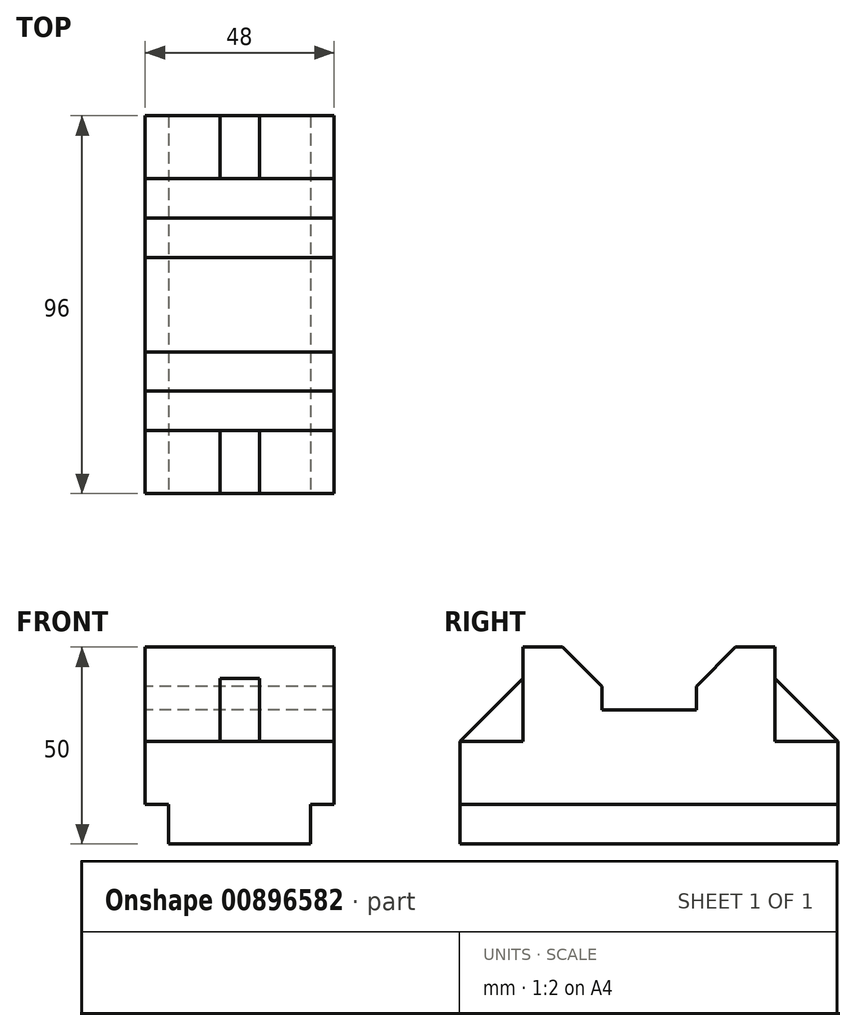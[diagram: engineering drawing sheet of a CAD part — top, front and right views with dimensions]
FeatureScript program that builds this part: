
annotation { "Feature Type Name" : "Feature", "Feature Type Description" : "" }
export const myFeature = defineFeature(function(context is Context, id is Id, definition is map)
    precondition{}
    {
        {
            var Q0;
            Q0=qCreatedBy(makeId("Front.planeOp"),FACE);
            var sketch = newSketch(context, id + "F0", { "sketchPlane" : qUnion([Q0])});
            skLineSegment(sketch, "E0.bottom", {"start": v(-24, 25) * mm, "end": v(24, 25) * mm});
            skLineSegment(sketch, "E0.top", {"start": v(-24, -25) * mm, "end": v(24, -25) * mm});
            skLineSegment(sketch, "E0.left", {"start": v(-24, 25) * mm, "end": v(-24, -25) * mm});
            skLineSegment(sketch, "E0.right", {"start": v(24, 25) * mm, "end": v(24, -25) * mm});
            skSolve(sketch);
        }
        {
            var Q0;
            Q0 = qSketchRegion(id + "F0", true);
            extrude(context, id + "F1", {"entities" : qUnion([Q0]), "endBound" : BoundingType.SYMMETRIC, "depth" : 96 * mm, "offsetDistance" : 25 * mm});
        }
        {
            var Q0;
            Q0=makeQuery(id+"F1.opExtrude","CAP_FACE",FACE,{"disambiguationData":[OSD([sQuery(id+"F0.wireOp",EDGE,"E0.bottom"),sQuery(id+"F0.wireOp",EDGE,"E0.top"),sQuery(id+"F0.wireOp",EDGE,"E0.left"),sQuery(id+"F0.wireOp",EDGE,"E0.right")])],"isStart":false});
            var sketch = newSketch(context, id + "F2", { "sketchPlane" : qUnion([Q0])});
            skLineSegment(sketch, "E1.bottom", {"start": v(-24, -25) * mm, "end": v(-18, -25) * mm});
            skLineSegment(sketch, "E1.top", {"start": v(-24, -15) * mm, "end": v(-18, -15) * mm});
            skLineSegment(sketch, "E1.left", {"start": v(-24, -25) * mm, "end": v(-24, -15) * mm});
            skLineSegment(sketch, "E1.right", {"start": v(-18, -25) * mm, "end": v(-18, -15) * mm});
            skLineSegment(sketch, "E2.bottom", {"start": v(24, -25) * mm, "end": v(18, -25) * mm});
            skLineSegment(sketch, "E2.top", {"start": v(24, -15) * mm, "end": v(18, -15) * mm});
            skLineSegment(sketch, "E2.left", {"start": v(24, -25) * mm, "end": v(24, -15) * mm});
            skLineSegment(sketch, "E2.right", {"start": v(18, -25) * mm, "end": v(18, -15) * mm});
            skSolve(sketch);
        }
        {
            var Q0;
            Q0 = qSketchRegion(id + "F2", true);
            extrude(context, id + "F3", {"entities" : qUnion([Q0]), "operationType" : NewBodyOperationType.REMOVE, "endBound" : BoundingType.THROUGH_ALL, "oppositeDirection" : true, "depth" : 25 * mm, "offsetDistance" : 25 * mm});
        }
        {
            var Q0;
            Q0=makeQuery(id+"F1.opExtrude","CAP_FACE",FACE,{"disambiguationData":[OSD([sQuery(id+"F0.wireOp",EDGE,"E0.bottom"),sQuery(id+"F0.wireOp",EDGE,"E0.top"),sQuery(id+"F0.wireOp",EDGE,"E0.left"),sQuery(id+"F0.wireOp",EDGE,"E0.right")])],"isStart":false});
            var sketch = newSketch(context, id + "F4", { "sketchPlane" : qUnion([Q0])});
            skLineSegment(sketch, "E3", {"start": v(-24, 1) * mm, "end": v(-5, 1) * mm});
            skLineSegment(sketch, "E4", {"start": v(-5, 1) * mm, "end": v(-5, 25) * mm});
            skLineSegment(sketch, "E5", {"start": v(-5, 25) * mm, "end": v(-24, 25) * mm});
            skLineSegment(sketch, "E6", {"start": v(-24, 25) * mm, "end": v(-24, 1) * mm});
            skLineSegment(sketch, "E7", {"start": v(-5, 1) * mm, "end": v(5, 1) * mm, "construction": true});
            skLineSegment(sketch, "E8", {"start": v(5, 1) * mm, "end": v(24, 1) * mm});
            skLineSegment(sketch, "E9", {"start": v(24, 1) * mm, "end": v(24, 25) * mm});
            skLineSegment(sketch, "E10", {"start": v(24, 25) * mm, "end": v(5, 25) * mm});
            skLineSegment(sketch, "E11", {"start": v(5, 25) * mm, "end": v(5, 1) * mm});
            skSolve(sketch);
        }
        {
            var Q0;
            Q0 = qSketchRegion(id + "F4", true);
            extrude(context, id + "F5", {"entities" : qUnion([Q0]), "operationType" : NewBodyOperationType.REMOVE, "oppositeDirection" : true, "depth" : 16 * mm, "offsetDistance" : 25 * mm});
        }
        {
            var Q0;
            Q0=makeQuery(id+"F5.boolean.opBoolean","COPY",FACE,{"derivedFrom":makeQuery(id+"F5.opExtrude","SWEPT_FACE",FACE,{"disambiguationData":[OSD([sQuery(id+"F4.wireOp",EDGE,"E4")])]})});
            var sketch = newSketch(context, id + "F6", { "sketchPlane" : qUnion([Q0])});
            skLineSegment(sketch, "E12", {"start": v(32, 1) * mm, "end": v(48, 1) * mm, "construction": true});
            skLineSegment(sketch, "E13", {"start": v(48, 1) * mm, "end": v(32, 17) * mm});
            skLineSegment(sketch, "E14", {"start": v(32, 17) * mm, "end": v(32, 1) * mm, "construction": true});
            skLineSegment(sketch, "E15", {"start": v(48, 1) * mm, "end": v(48, 25) * mm});
            skLineSegment(sketch, "E16", {"start": v(48, 25) * mm, "end": v(32, 25) * mm});
            skLineSegment(sketch, "E17", {"start": v(32, 25) * mm, "end": v(32, 17) * mm});
            skSolve(sketch);
        }
        {
            var Q0;
            Q0 = qSketchRegion(id + "F6", true);
            extrude(context, id + "F7", {"entities" : qUnion([Q0]), "operationType" : NewBodyOperationType.REMOVE, "endBound" : BoundingType.THROUGH_ALL, "oppositeDirection" : true, "depth" : 25 * mm, "offsetDistance" : 25 * mm});
        }
        {
            var Q0;
            Q0=makeQuery(id+"F1.opExtrude","SWEPT_FACE",FACE,{"disambiguationData":[OSD([sQuery(id+"F0.wireOp",EDGE,"E0.left")])]});
            var sketch = newSketch(context, id + "F8", { "sketchPlane" : qUnion([Q0])});
            skLineSegment(sketch, "E18", {"start": v(32, 25) * mm, "end": v(22, 25) * mm, "construction": true});
            skLineSegment(sketch, "E19", {"start": v(22, 25) * mm, "end": v(12, 25) * mm, "construction": true});
            skLineSegment(sketch, "E20", {"start": v(12, 25) * mm, "end": v(12, 15) * mm, "construction": true});
            skLineSegment(sketch, "E21", {"start": v(22, 25) * mm, "end": v(12, 15) * mm});
            skLineSegment(sketch, "E22", {"start": v(12, 15) * mm, "end": v(12, 9) * mm});
            skLineSegment(sketch, "E23", {"start": v(12, 9) * mm, "end": v(-12, 9) * mm});
            skLineSegment(sketch, "E24", {"start": v(12, 15) * mm, "end": v(-12, 15) * mm, "construction": true});
            skLineSegment(sketch, "E25", {"start": v(-12, 9) * mm, "end": v(-12, 15) * mm});
            skLineSegment(sketch, "E26", {"start": v(-12, 15) * mm, "end": v(-12, 25) * mm, "construction": true});
            skLineSegment(sketch, "E27", {"start": v(-12, 25) * mm, "end": v(-22, 25) * mm, "construction": true});
            skLineSegment(sketch, "E28", {"start": v(-12, 15) * mm, "end": v(-22, 25) * mm});
            skLineSegment(sketch, "E29", {"start": v(-22, 25) * mm, "end": v(22, 25) * mm});
            skSolve(sketch);
        }
        {
            var Q0;
            Q0 = qSketchRegion(id + "F8", true);
            extrude(context, id + "F9", {"entities" : qUnion([Q0]), "operationType" : NewBodyOperationType.REMOVE, "endBound" : BoundingType.THROUGH_ALL, "oppositeDirection" : true, "depth" : 25 * mm, "offsetDistance" : 25 * mm});
        }
        {
            var Q0;
            Q0=makeQuery(id+"F1.opExtrude","CAP_FACE",FACE,{"disambiguationData":[OSD([sQuery(id+"F0.wireOp",EDGE,"E0.bottom"),sQuery(id+"F0.wireOp",EDGE,"E0.top"),sQuery(id+"F0.wireOp",EDGE,"E0.left"),sQuery(id+"F0.wireOp",EDGE,"E0.right")])],"isStart":true});
            var sketch = newSketch(context, id + "F10", { "sketchPlane" : qUnion([Q0])});
            skLineSegment(sketch, "E30.bottom", {"start": v(-24, 25) * mm, "end": v(-5, 25) * mm});
            skLineSegment(sketch, "E30.top", {"start": v(-24, 1) * mm, "end": v(-5, 1) * mm});
            skLineSegment(sketch, "E30.left", {"start": v(-24, 25) * mm, "end": v(-24, 1) * mm});
            skLineSegment(sketch, "E30.right", {"start": v(-5, 25) * mm, "end": v(-5, 1) * mm});
            skLineSegment(sketch, "E31.bottom", {"start": v(24, 25) * mm, "end": v(5, 25) * mm});
            skLineSegment(sketch, "E31.top", {"start": v(24, 1) * mm, "end": v(5, 1) * mm});
            skLineSegment(sketch, "E31.left", {"start": v(24, 25) * mm, "end": v(24, 1) * mm});
            skLineSegment(sketch, "E31.right", {"start": v(5, 25) * mm, "end": v(5, 1) * mm});
            skSolve(sketch);
        }
        {
            var Q0;
            Q0 = qSketchRegion(id + "F10", true);
            extrude(context, id + "F11", {"entities" : qUnion([Q0]), "operationType" : NewBodyOperationType.REMOVE, "oppositeDirection" : true, "depth" : 16 * mm, "offsetDistance" : 25 * mm});
        }
        {
            var Q0;
            Q0=makeQuery(id+"F11.boolean.opBoolean","COPY",FACE,{"derivedFrom":makeQuery(id+"F11.opExtrude","SWEPT_FACE",FACE,{"disambiguationData":[OSD([sQuery(id+"F10.wireOp",EDGE,"E31.right")])]})});
            var sketch = newSketch(context, id + "F12", { "sketchPlane" : qUnion([Q0])});
            skLineSegment(sketch, "E32", {"start": v(-48, 1) * mm, "end": v(-32, 1) * mm, "construction": true});
            skLineSegment(sketch, "E33", {"start": v(-32, 1) * mm, "end": v(-32, 17) * mm, "construction": true});
            skLineSegment(sketch, "E34", {"start": v(-32, 17) * mm, "end": v(-48, 1) * mm});
            skLineSegment(sketch, "E35", {"start": v(-48, 1) * mm, "end": v(-48, 25) * mm});
            skLineSegment(sketch, "E36", {"start": v(-48, 25) * mm, "end": v(-32, 25) * mm});
            skLineSegment(sketch, "E37", {"start": v(-32, 25) * mm, "end": v(-32, 17) * mm});
            skSolve(sketch);
        }
        {
            var Q0;
            Q0 = qSketchRegion(id + "F12", true);
            extrude(context, id + "F13", {"entities" : qUnion([Q0]), "operationType" : NewBodyOperationType.REMOVE, "endBound" : BoundingType.THROUGH_ALL, "oppositeDirection" : true, "depth" : 25 * mm, "offsetDistance" : 25 * mm});
        }
    });
